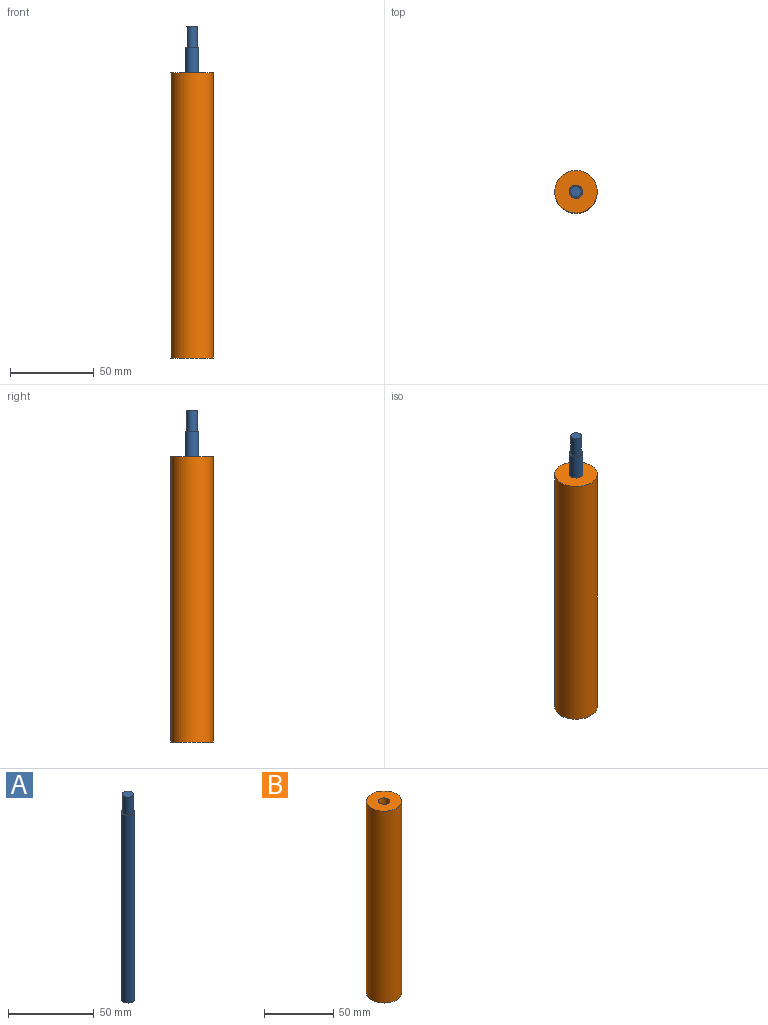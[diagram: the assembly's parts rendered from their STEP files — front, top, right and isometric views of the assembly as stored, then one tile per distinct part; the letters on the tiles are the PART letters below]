
ASSEMBLY  parts=2 mates=1
PART A: 5 faces, bbox 7.9x7.9x146.1 mm
  f0: cylinder r=3.97mm len=133.35mm, axis (0,0,-1), area 3325.3mm2, adj f1,f2
  f1: plane 7.94x7.94mm, normal (0,0,1), area 17.8mm2, adj f0,f3
  f2: plane 7.94x7.94mm, normal (0,0,-1), area 49.5mm2, adj f0
  f3: cylinder r=3.17mm len=12.7mm, axis (0,0,-1), area 253.4mm2, adj f1,f4
  f4: plane 6.35x6.35mm, normal (0,0,1), area 31.7mm2, adj f3
PART B: 5 faces, bbox 25.4x25.4x169.9 mm
  f0: cylinder r=12.7mm len=169.86mm, axis (0,0,-1), area 13554.4mm2, adj f1,f2
  f1: plane 25.4x25.4mm, normal (0,0,1), area 457.2mm2, adj f0,f3
  f2: plane 25.4x25.4mm, normal (0,0,-1), area 506.7mm2, adj f0
  f3: cylinder r=3.97mm len=101.6mm, axis (0,0,1), area 2533.5mm2, adj f1,f4
  f4: plane 7.94x7.94mm, normal (0,0,1), area 49.5mm2, adj f3
PLACE A t=(49.84,30.41,20.37)mm
PLACE B t=(49.84,30.41,-31.41)mm
MATE cylindrical A.f0 <-> B.f3  axis (0,0,-1) through (49.84,30.41,87.05)mm
